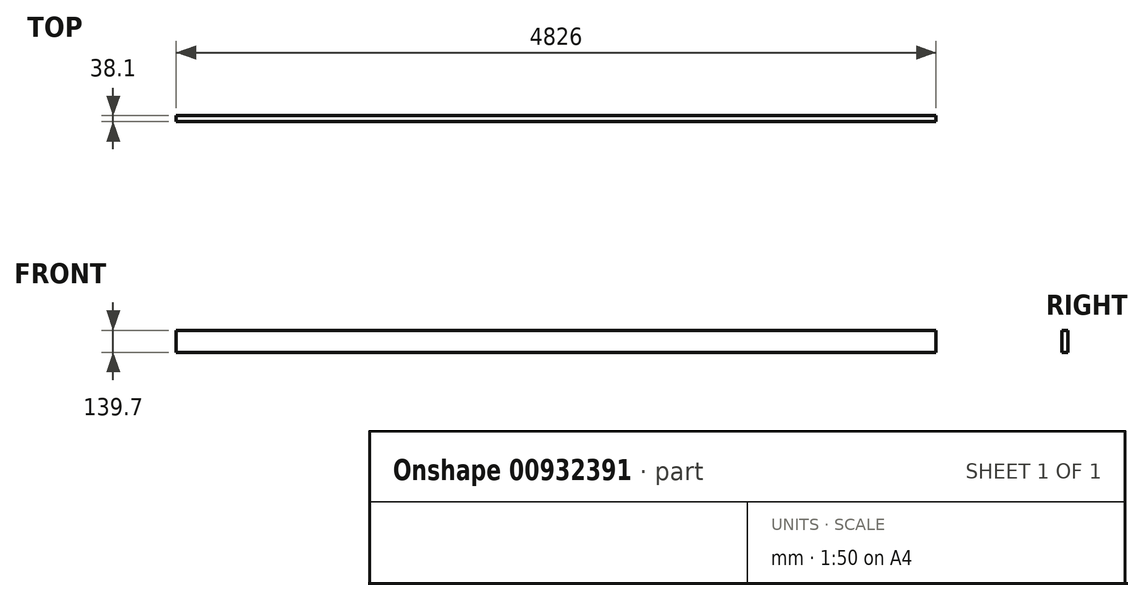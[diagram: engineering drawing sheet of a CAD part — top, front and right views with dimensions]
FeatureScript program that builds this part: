
annotation { "Feature Type Name" : "Feature", "Feature Type Description" : "" }
export const myFeature = defineFeature(function(context is Context, id is Id, definition is map)
    precondition{}
    {
        {
            var Q0;
            Q0=qCreatedBy(makeId("Right.planeOp"),FACE);
            var sketch = newSketch(context, id + "F0", { "sketchPlane" : qUnion([Q0])});
            skLineSegment(sketch, "E0.bottom", {"start": v(19.05, 69.85) * mm, "end": v(-19.05, 69.85) * mm});
            skLineSegment(sketch, "E0.top", {"start": v(19.05, -69.85) * mm, "end": v(-19.05, -69.85) * mm});
            skLineSegment(sketch, "E0.left", {"start": v(19.05, 69.85) * mm, "end": v(19.05, -69.85) * mm});
            skLineSegment(sketch, "E0.right", {"start": v(-19.05, 69.85) * mm, "end": v(-19.05, -69.85) * mm});
            skPoint(sketch, "E0.middle", {"position": v(0, 0) * mm});
            skSolve(sketch);
        }
        {
            var Q0;
            Q0=makeQuery(id+"F0.imprint","IMPRINT",FACE,{"disambiguationData":[TD([[makeQuery(id+"F0.imprint","IMPRINT",EDGE,{"derivedFrom":sQuery(id+"F0.wireOp",EDGE,"E0.bottom")}),1.0]])]});
            extrude(context, id + "F1", {"entities" : qUnion([Q0]), "depth" : 4826 * mm, "offsetDistance" : 25.4 * mm});
        }
    });
